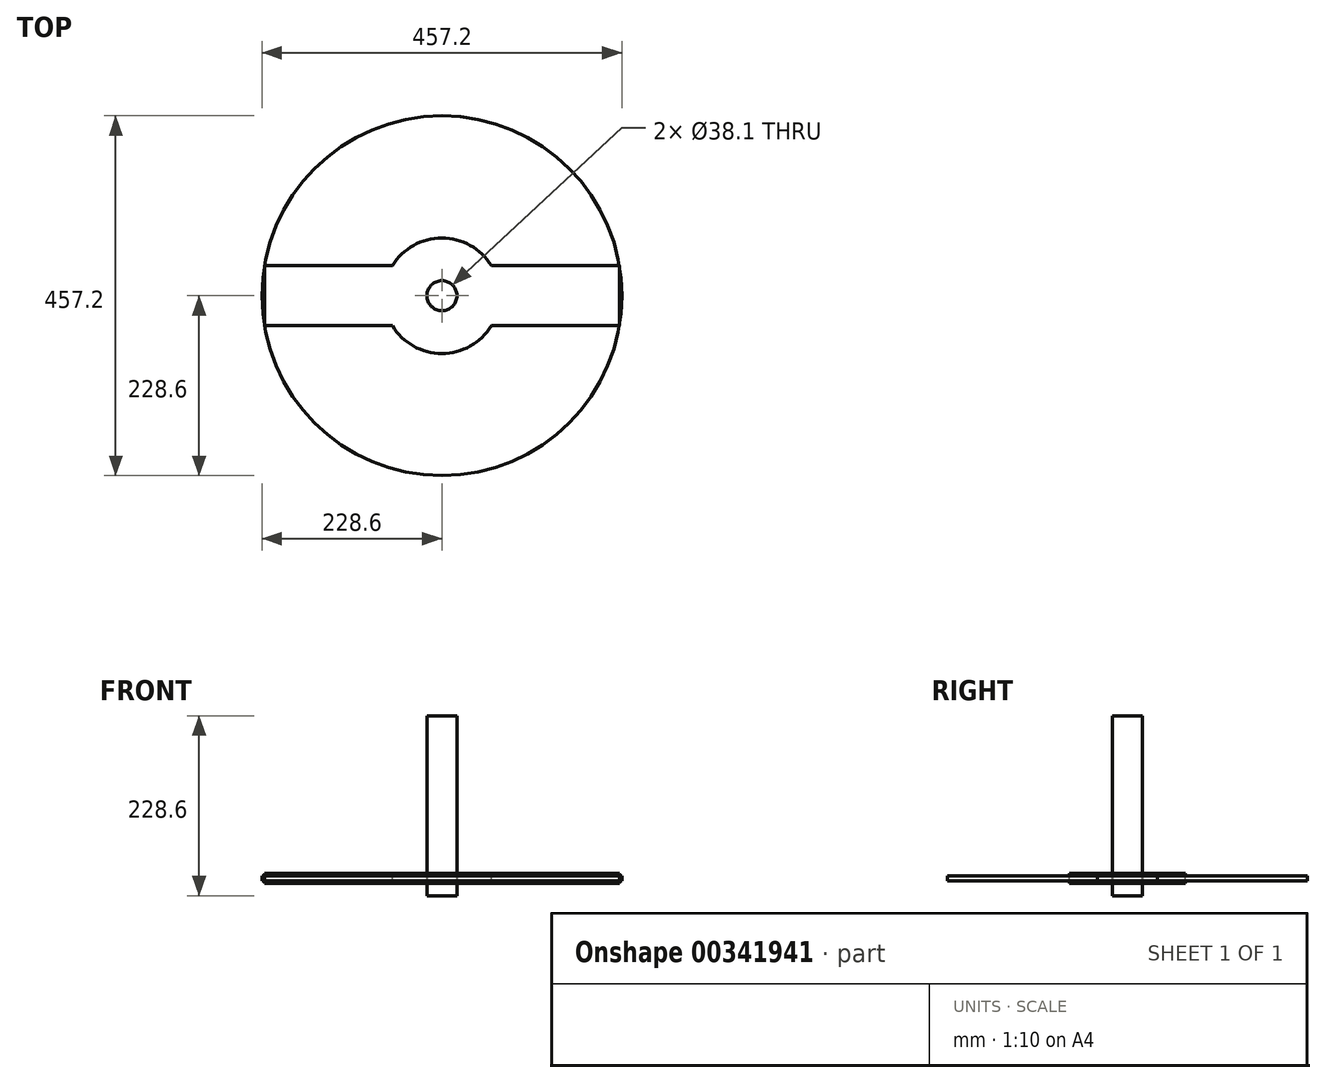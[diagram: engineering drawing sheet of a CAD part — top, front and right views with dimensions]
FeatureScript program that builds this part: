
annotation { "Feature Type Name" : "Feature", "Feature Type Description" : "" }
export const myFeature = defineFeature(function(context is Context, id is Id, definition is map)
    precondition{}
    {
        {
            var Q0;
            Q0=qCreatedBy(makeId("Top.planeOp"),FACE);
            var sketch = newSketch(context, id + "F0", { "sketchPlane" : qUnion([Q0])});
            skCircle(sketch, "E0", {"center": v(0, 0) * mm, "radius": 228.6 * mm});
            skCircle(sketch, "E1", {"center": v(0, 0) * mm, "radius": 19.05 * mm});
            skSolve(sketch);
        }
        {
            var Q0;
            Q0=makeQuery(id+"F0.imprint","IMPRINT",FACE,{"disambiguationData":[TD([[makeQuery(id+"F0.imprint","IMPRINT",EDGE,{"derivedFrom":sQuery(id+"F0.wireOp",EDGE,"E0")}),1.0]])]});
            extrude(context, id + "F1", {"entities" : qUnion([Q0]), "oppositeDirection" : true, "depth" : 6.35 * mm});
        }
        {
            var Q0;
            Q0=makeQuery(id+"F0.imprint","IMPRINT",FACE,{"disambiguationData":[TD([[makeQuery(id+"F0.imprint","IMPRINT",EDGE,{"derivedFrom":sQuery(id+"F0.wireOp",EDGE,"E1")}),1.0]])]});
            extrude(context, id + "F2", {"entities" : qUnion([Q0]), "depth" : 203.2 * mm, "hasSecondDirection" : true, "secondDirectionOppositeDirection" : true, "secondDirectionDepth" : 25.4 * mm});
        }
        {
            var Q0;
            Q0=makeQuery(id+"F0.imprint","IMPRINT",FACE,{"disambiguationData":[TD([[makeQuery(id+"F0.imprint","IMPRINT",EDGE,{"derivedFrom":sQuery(id+"F0.wireOp",EDGE,"E0")}),1.0]])]});
            var sketch = newSketch(context, id + "F3", { "sketchPlane" : qUnion([Q0])});
            skArc(sketch, "E2", {"start": v(-62.77, -38.1) * mm, "mid": v(0, -73.43) * mm, "end": v(62.77, -38.1) * mm});
            skLineSegment(sketch, "E3.bottom", {"start": v(-225.4, -38.1) * mm, "end": v(-62.77, -38.1) * mm});
            skLineSegment(sketch, "E3.top", {"start": v(-225.4, 38.1) * mm, "end": v(-62.77, 38.1) * mm});
            skLineSegment(sketch, "E3.left", {"start": v(-225.4, -38.1) * mm, "end": v(-225.4, 38.1) * mm});
            skLineSegment(sketch, "E3.right", {"start": v(225.4, -38.1) * mm, "end": v(225.4, 38.1) * mm});
            skLineSegment(sketch, "E4.trimOffspring", {"start": v(62.77, -38.1) * mm, "end": v(225.4, -38.1) * mm});
            skLineSegment(sketch, "E5.trimOffspring", {"start": v(62.77, 38.1) * mm, "end": v(225.4, 38.1) * mm});
            skArc(sketch, "E6.trimOffspring", {"start": v(62.77, 38.1) * mm, "mid": v(0, 73.43) * mm, "end": v(-62.77, 38.1) * mm});
            skSolve(sketch);
        }
        {
            var Q0;
            Q0=makeQuery(id+"F3.imprint","IMPRINT",FACE,{"disambiguationData":[TD([[makeQuery(id+"F3.imprint","IMPRINT",EDGE,{"derivedFrom":sQuery(id+"F3.wireOp",EDGE,"E2")}),1.0]])]});
            extrude(context, id + "F4", {"entities" : qUnion([Q0]), "oppositeDirection" : true, "depth" : 9.52 * mm, "hasSecondDirection" : true, "secondDirectionOppositeDirection" : false, "secondDirectionDepth" : 3.17 * mm});
        }
    });
